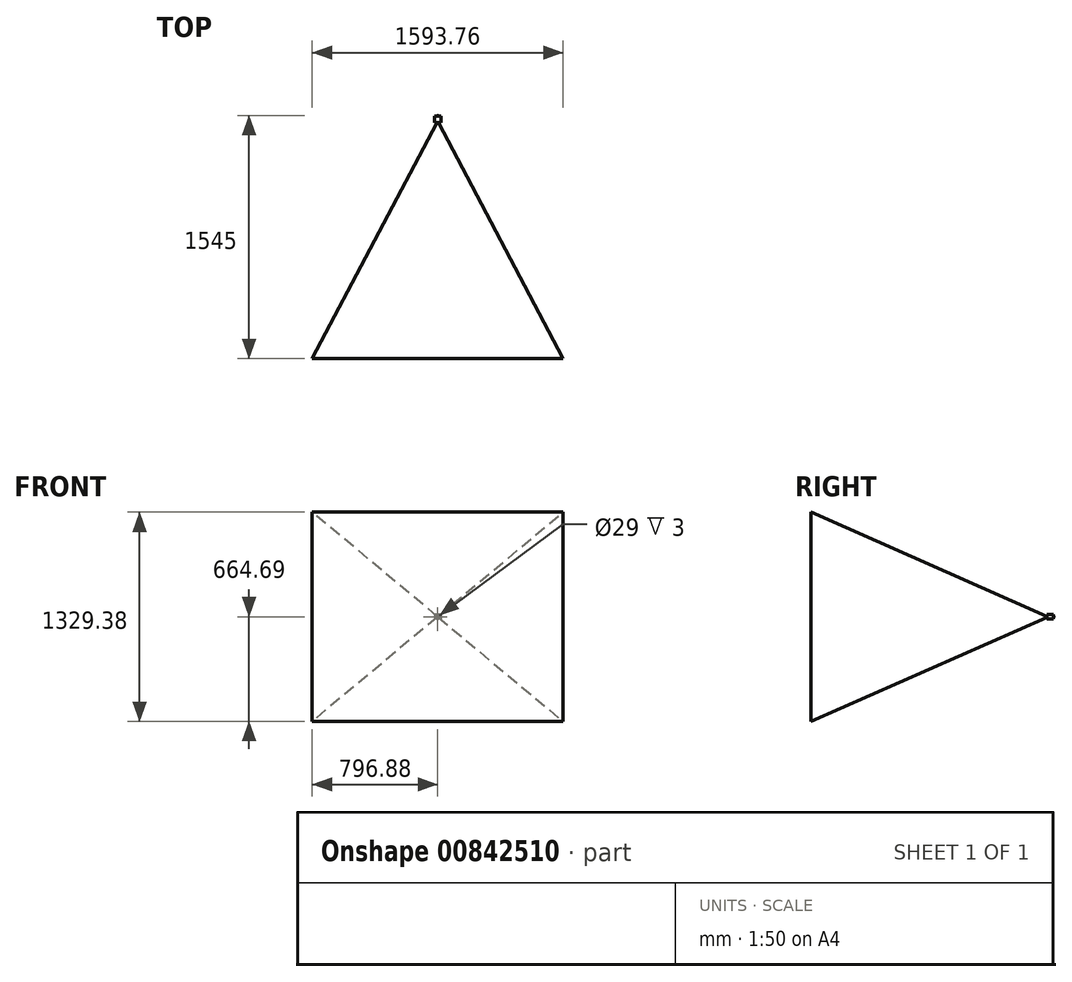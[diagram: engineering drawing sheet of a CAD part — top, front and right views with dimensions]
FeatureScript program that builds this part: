
annotation { "Feature Type Name" : "Feature", "Feature Type Description" : "" }
export const myFeature = defineFeature(function(context is Context, id is Id, definition is map)
    precondition{}
    {
        {
            var Q0;
            Q0=qCreatedBy(makeId("Front.planeOp"),FACE);
            var sketch = newSketch(context, id + "F0", { "sketchPlane" : qUnion([Q0])});
            skLineSegment(sketch, "E0.bottom", {"start": v(20, 15) * mm, "end": v(-20, 15) * mm});
            skLineSegment(sketch, "E0.top", {"start": v(20, -15) * mm, "end": v(-20, -15) * mm});
            skLineSegment(sketch, "E0.left", {"start": v(20, 15) * mm, "end": v(20, -15) * mm});
            skLineSegment(sketch, "E0.right", {"start": v(-20, 15) * mm, "end": v(-20, -15) * mm});
            skPoint(sketch, "E0.middle", {"position": v(0, 0) * mm});
            skSolve(sketch);
        }
        {
            var Q0;
            Q0=qSketchRegion(id+"F0",true);
            extrude(context, id + "F1", {"entities" : qUnion([Q0]), "depth" : 40 * mm, "offsetDistance" : 25 * mm});
        }
        {
            assignVariable(context, id + "F2", {"name" : "WorkingDistance", "anyValue" : 1500});
        }
        {
            var Q0;
            Q0=makeQuery(id+"F1.opExtrude","CAP_FACE",FACE,{"disambiguationData":[OSD([sQuery(id+"F0.wireOp",EDGE,"E0.bottom"),sQuery(id+"F0.wireOp",EDGE,"E0.top"),sQuery(id+"F0.wireOp",EDGE,"E0.left"),sQuery(id+"F0.wireOp",EDGE,"E0.right")])],"isStart":false});
            var sketch = newSketch(context, id + "F3", { "sketchPlane" : qUnion([Q0])});
            skCircle(sketch, "E1", {"center": v(0, 0) * mm, "radius": 14.5 * mm});
            skSolve(sketch);
        }
        {
            var Q0;
            Q0=qSketchRegion(id+"F3",true);
            extrude(context, id + "F4", {"entities" : qUnion([Q0]), "operationType" : NewBodyOperationType.REMOVE, "oppositeDirection" : true, "depth" : 3 * mm, "offsetDistance" : 25 * mm});
        }
        {
            var Q0;
            Q0=makeQuery(id+"F4.boolean.opBoolean","COPY",FACE,{"derivedFrom":makeQuery(id+"F4.opExtrude","CAP_FACE",FACE,{"disambiguationData":[OSD([sQuery(id+"F3.wireOp",EDGE,"E1")])],"isStart":false})});
            var sketch = newSketch(context, id + "F5", { "sketchPlane" : qUnion([Q0])});
            skLineSegment(sketch, "E2.bottom", {"start": v(4.25, 3.54) * mm, "end": v(-4.25, 3.54) * mm});
            skLineSegment(sketch, "E2.top", {"start": v(4.25, -3.54) * mm, "end": v(-4.25, -3.54) * mm});
            skLineSegment(sketch, "E2.left", {"start": v(4.25, 3.54) * mm, "end": v(4.25, -3.54) * mm});
            skLineSegment(sketch, "E2.right", {"start": v(-4.25, 3.54) * mm, "end": v(-4.25, -3.54) * mm});
            skPoint(sketch, "E2.middle", {"position": v(0, 0) * mm});
            skSolve(sketch);
        }
        {
            var Q0;
            Q0=qSketchRegion(id+"F5",true);
            extrude(context, id + "F6", {"entities" : qUnion([Q0]), "operationType" : NewBodyOperationType.ADD, "depth" : 3 * mm, "offsetDistance" : 25 * mm});
        }
        {
            var Q0;
            Q0=makeQuery(id+"F6.opExtrude","CAP_FACE",FACE,{"disambiguationData":[OSD([sQuery(id+"F5.wireOp",EDGE,"E2.bottom"),sQuery(id+"F5.wireOp",EDGE,"E2.top"),sQuery(id+"F5.wireOp",EDGE,"E2.left"),sQuery(id+"F5.wireOp",EDGE,"E2.right")])],"isStart":false});
            cPlane(context, id + "F7", {"entities" : qUnion([Q0]), "cplaneType" : CPlaneType.OFFSET, "offset" : (getVariable(context, 'WorkingDistance')) * mm, "width" : 150 * mm, "height" : 150 * mm});
        }
        {
            var Q0;
            Q0=qCreatedBy(id+"F7.planeOp",FACE);
            var sketch = newSketch(context, id + "F8", { "sketchPlane" : qUnion([Q0])});
            skLineSegment(sketch, "E3.bottom", {"start": v(796.88, 664.69) * mm, "end": v(-796.87, 664.69) * mm});
            skLineSegment(sketch, "E3.top", {"start": v(796.87, -664.69) * mm, "end": v(-796.88, -664.69) * mm});
            skLineSegment(sketch, "E3.left", {"start": v(796.88, 664.69) * mm, "end": v(796.87, -664.69) * mm});
            skLineSegment(sketch, "E3.right", {"start": v(-796.87, 664.69) * mm, "end": v(-796.88, -664.69) * mm});
            skPoint(sketch, "E3.middle", {"position": v(0, 0) * mm});
            skSolve(sketch);
        }
        {
            var Q1;
            Q1=makeQuery(id+"F6.opExtrude","CAP_FACE",FACE,{"disambiguationData":[OSD([sQuery(id+"F5.wireOp",EDGE,"E2.bottom"),sQuery(id+"F5.wireOp",EDGE,"E2.top"),sQuery(id+"F5.wireOp",EDGE,"E2.left"),sQuery(id+"F5.wireOp",EDGE,"E2.right")])],"isStart":false});
            var Q2;
            Q2=makeQuery(id+"F8.imprint","IMPRINT",FACE,{"disambiguationData":[TD([[makeQuery(id+"F8.imprint","IMPRINT",EDGE,{"derivedFrom":sQuery(id+"F8.wireOp",EDGE,"E3.bottom")}),1.0]])]});
            loft(context, id + "F9", {"operationType" : NewBodyOperationType.ADD, "sheetProfilesArray" : [{ "sheetProfileEntities" : qUnion([Q1]) }, { "sheetProfileEntities" : qUnion([Q2]) }]});
        }
        {
            var Q0;
            Q0=makeQuery(id+"F0.imprint","IMPRINT",FACE,{"disambiguationData":[TD([[makeQuery(id+"F0.imprint","IMPRINT",EDGE,{"derivedFrom":sQuery(id+"F0.wireOp",EDGE,"E0.bottom")}),1.0]])]});
            var sketch = newSketch(context, id + "F10", { "sketchPlane" : qUnion([Q0])});
            skArc(sketch, "E4", {"start": v(0, 5) * mm, "mid": v(5, 0) * mm, "end": v(0, -5) * mm});
            skLineSegment(sketch, "E5", {"start": v(0, 5) * mm, "end": v(0, -5) * mm});
            skSolve(sketch);
        }
        {
            var Q0;
            Q0=qSketchRegion(id+"F10",true);
            var Q1;
            Q1=sQuery(id+"F10.wireOp",EDGE,"E5");
            revolve(context, id + "F11", {"operationType" : NewBodyOperationType.ADD, "surfaceOperationType" : NewSurfaceOperationType.NEW, "entities" : qUnion([Q0]), "axis" : qUnion([Q1]), "revolveType" : RevolveType.FULL});
        }
    });
